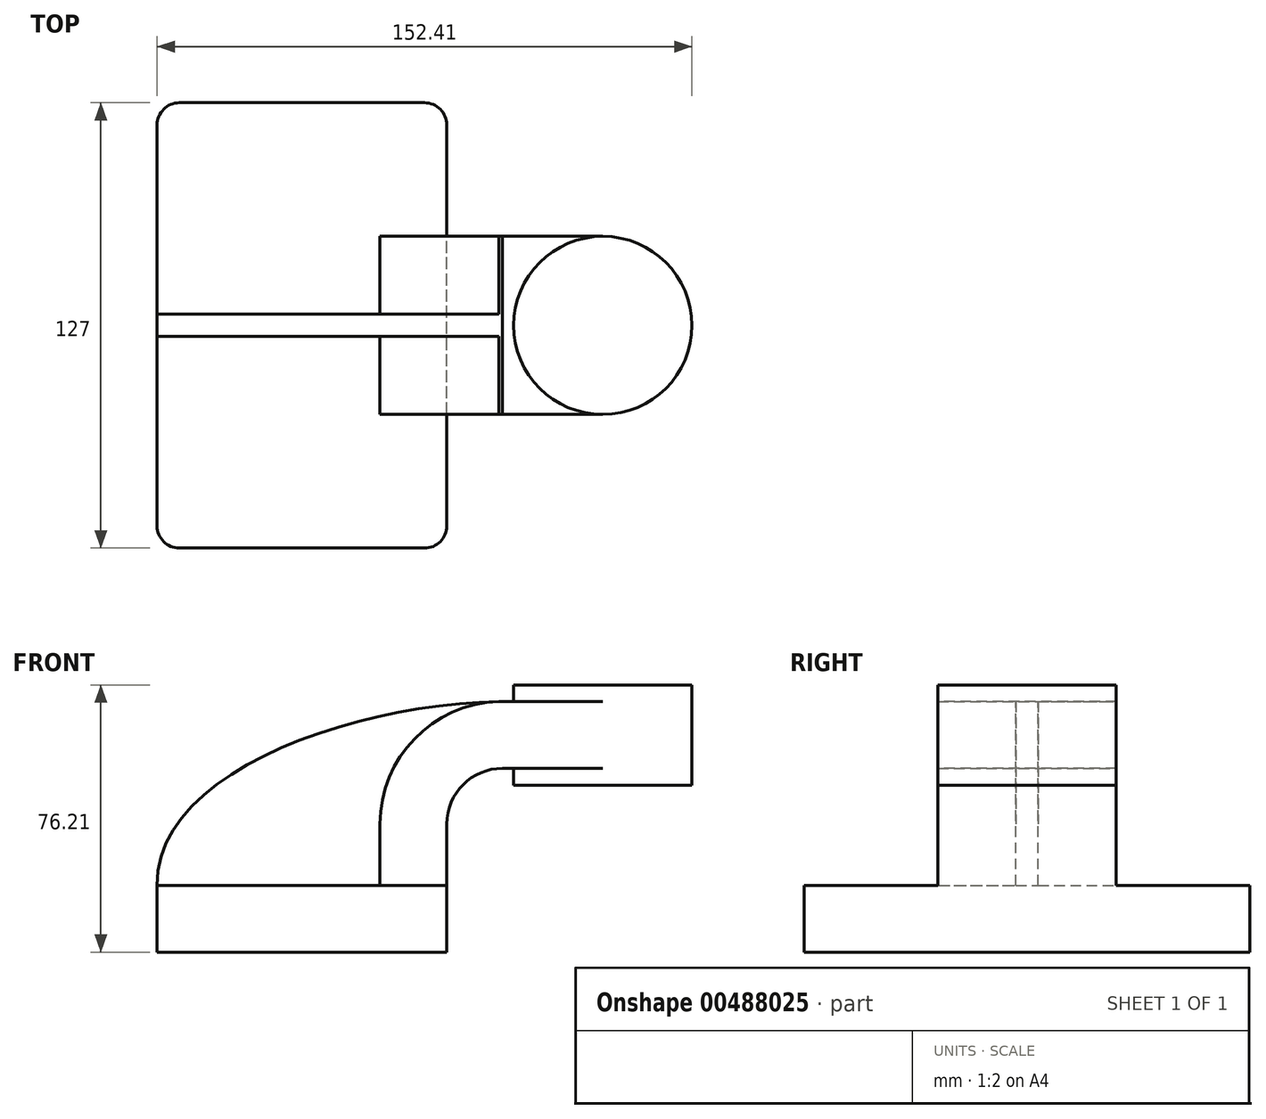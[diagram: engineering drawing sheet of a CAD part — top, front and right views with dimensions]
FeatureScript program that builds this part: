
annotation { "Feature Type Name" : "Feature", "Feature Type Description" : "" }
export const myFeature = defineFeature(function(context is Context, id is Id, definition is map)
    precondition{}
    {
        {
            var Q0;
            Q0=qCreatedBy(makeId("Front.planeOp"),FACE);
            var sketch = newSketch(context, id + "F0", { "sketchPlane" : qUnion([Q0])});
            skLineSegment(sketch, "E0.bottom", {"start": v(41.28, 9.53) * mm, "end": v(-41.28, 9.53) * mm});
            skLineSegment(sketch, "E0.top", {"start": v(41.28, -9.52) * mm, "end": v(-41.28, -9.52) * mm});
            skLineSegment(sketch, "E0.left", {"start": v(41.28, 9.53) * mm, "end": v(41.28, -9.52) * mm});
            skLineSegment(sketch, "E0.right", {"start": v(-41.28, 9.53) * mm, "end": v(-41.28, -9.52) * mm});
            skPoint(sketch, "E0.middle", {"position": v(0, 0) * mm});
            skLineSegment(sketch, "E1.bottom", {"start": v(111.13, 38.1) * mm, "end": v(60.33, 38.1) * mm});
            skLineSegment(sketch, "E1.top", {"start": v(111.13, 66.68) * mm, "end": v(60.33, 66.68) * mm});
            skLineSegment(sketch, "E1.left", {"start": v(111.13, 38.1) * mm, "end": v(111.13, 66.68) * mm});
            skLineSegment(sketch, "E1.right", {"start": v(60.33, 38.1) * mm, "end": v(60.33, 66.68) * mm});
            skPoint(sketch, "E1.middle", {"position": v(85.73, 52.39) * mm});
            skLineSegment(sketch, "E2", {"start": v(41.28, 9.53) * mm, "end": v(41.28, 27) * mm});
            skArc(sketch, "E3", {"start": v(41.27, 27) * mm, "mid": v(45.92, 38.23) * mm, "end": v(57.15, 42.88) * mm});
            skLineSegment(sketch, "E4", {"start": v(57.15, 42.88) * mm, "end": v(85.72, 42.88) * mm});
            skLineSegment(sketch, "E5.0", {"start": v(57.15, 61.93) * mm, "end": v(85.72, 61.93) * mm});
            skArc(sketch, "E5.1", {"start": v(22.23, 27) * mm, "mid": v(32.45, 51.7) * mm, "end": v(57.15, 61.93) * mm});
            skLineSegment(sketch, "E5.2", {"start": v(22.23, 9.53) * mm, "end": v(22.23, 27) * mm});
            skLineSegment(sketch, "E6", {"start": v(85.72, 61.93) * mm, "end": v(85.72, 42.88) * mm});
            skFitSpline(sketch, "E7", {"points": [v(-41.28, 9.53) * mm, v(57.15, 61.93) * mm], "startDerivative": vector(-1.3, 97.86) * mm, "endDerivative": vector(126.06, 1.47) * mm});
            skLineSegment(sketch, "E8", {"start": v(85.73, 66.68) * mm, "end": v(85.73, 38.1) * mm});
            skSolve(sketch);
        }
        {
            var Q0;
            Q0=makeQuery(id+"F0.imprint","IMPRINT",FACE,{"disambiguationData":[TD([[makeQuery(id+"F0.imprint","IMPRINT",EDGE,{"derivedFrom":sQuery(id+"F0.wireOp",EDGE,"E0.top")}),-1.0]])]});
            extrude(context, id + "F1", {"entities" : qUnion([Q0]), "endBound" : BoundingType.SYMMETRIC, "depth" : 127 * mm});
        }
        {
            var Q0;
            {var subQ0=sQuery(id+"F0.wireOp",EDGE,"E4");var subQ1=sQuery(id+"F0.wireOp",EDGE,"E1.right");var subQ2=makeQuery(id+"F0.imprint","INTERSECT",VERTEX,{"derivedFrom":[subQ1,subQ0]});Q0=makeQuery(id+"F0.imprint","IMPRINT",FACE,{"disambiguationData":[TD([[makeQuery(id+"F0.imprint","IMPRINT",EDGE,{"disambiguationData":[TD([[subQ2,-1.0]])],"derivedFrom":subQ1}),-1.0]])]});}
            var Q1;
            {var subQ1=sQuery(id+"F0.wireOp",EDGE,"E2");Q1=makeQuery(id+"F0.imprint","IMPRINT",FACE,{"disambiguationData":[TD([[makeQuery(id+"F0.imprint","IMPRINT",EDGE,{"derivedFrom":subQ1}),1.0]])]});}
            extrude(context, id + "F2", {"entities" : qUnion([Q0, Q1]), "operationType" : NewBodyOperationType.ADD, "endBound" : BoundingType.SYMMETRIC, "depth" : 50.8 * mm});
        }
        {
            var Q0;
            {var subQ3=sQuery(id+"F0.wireOp",EDGE,"E5.2");Q0=makeQuery(id+"F0.imprint","IMPRINT",FACE,{"disambiguationData":[TD([[makeQuery(id+"F0.imprint","IMPRINT",EDGE,{"derivedFrom":subQ3}),1.0]])]});}
            extrude(context, id + "F3", {"entities" : qUnion([Q0]), "operationType" : NewBodyOperationType.ADD, "endBound" : BoundingType.SYMMETRIC, "depth" : 6.35 * mm});
        }
        {
            var Q0;
            {var subQ4=sQuery(id+"F0.wireOp",EDGE,"E1.left");Q0=makeQuery(id+"F0.imprint","IMPRINT",FACE,{"disambiguationData":[TD([[makeQuery(id+"F0.imprint","IMPRINT",EDGE,{"derivedFrom":subQ4}),1.0]])]});}
            var Q1;
            Q1=sQuery(id+"F0.wireOp",EDGE,"E8");
            revolve(context, id + "F4", {"operationType" : NewBodyOperationType.ADD, "entities" : qUnion([Q0]), "axis" : qUnion([Q1]), "revolveType" : RevolveType.FULL});
        }
        {
            var Q0;
            Q0=makeQuery(id+"F1.opExtrude","CAP_EDGE",EDGE,{"disambiguationData":[OSD([sQuery(id+"F0.wireOp",EDGE,"E0.right")])],"isStart":false});
            var Q1;
            Q1=makeQuery(id+"F1.opExtrude","CAP_EDGE",EDGE,{"disambiguationData":[OSD([sQuery(id+"F0.wireOp",EDGE,"E0.left")])],"isStart":false});
            var Q2;
            Q2=makeQuery(id+"F1.opExtrude","CAP_EDGE",EDGE,{"disambiguationData":[OSD([sQuery(id+"F0.wireOp",EDGE,"E0.right")])],"isStart":true});
            var Q3;
            Q3=makeQuery(id+"F1.opExtrude","CAP_EDGE",EDGE,{"disambiguationData":[OSD([sQuery(id+"F0.wireOp",EDGE,"E0.left")])],"isStart":true});
            fillet(context, id + "F5", {"entities" : qUnion([Q0, Q1, Q2, Q3]), "radius" : 6.35 * mm, "tangentPropagation" : true, "allowEdgeOverflow" : false});
        }
    });
